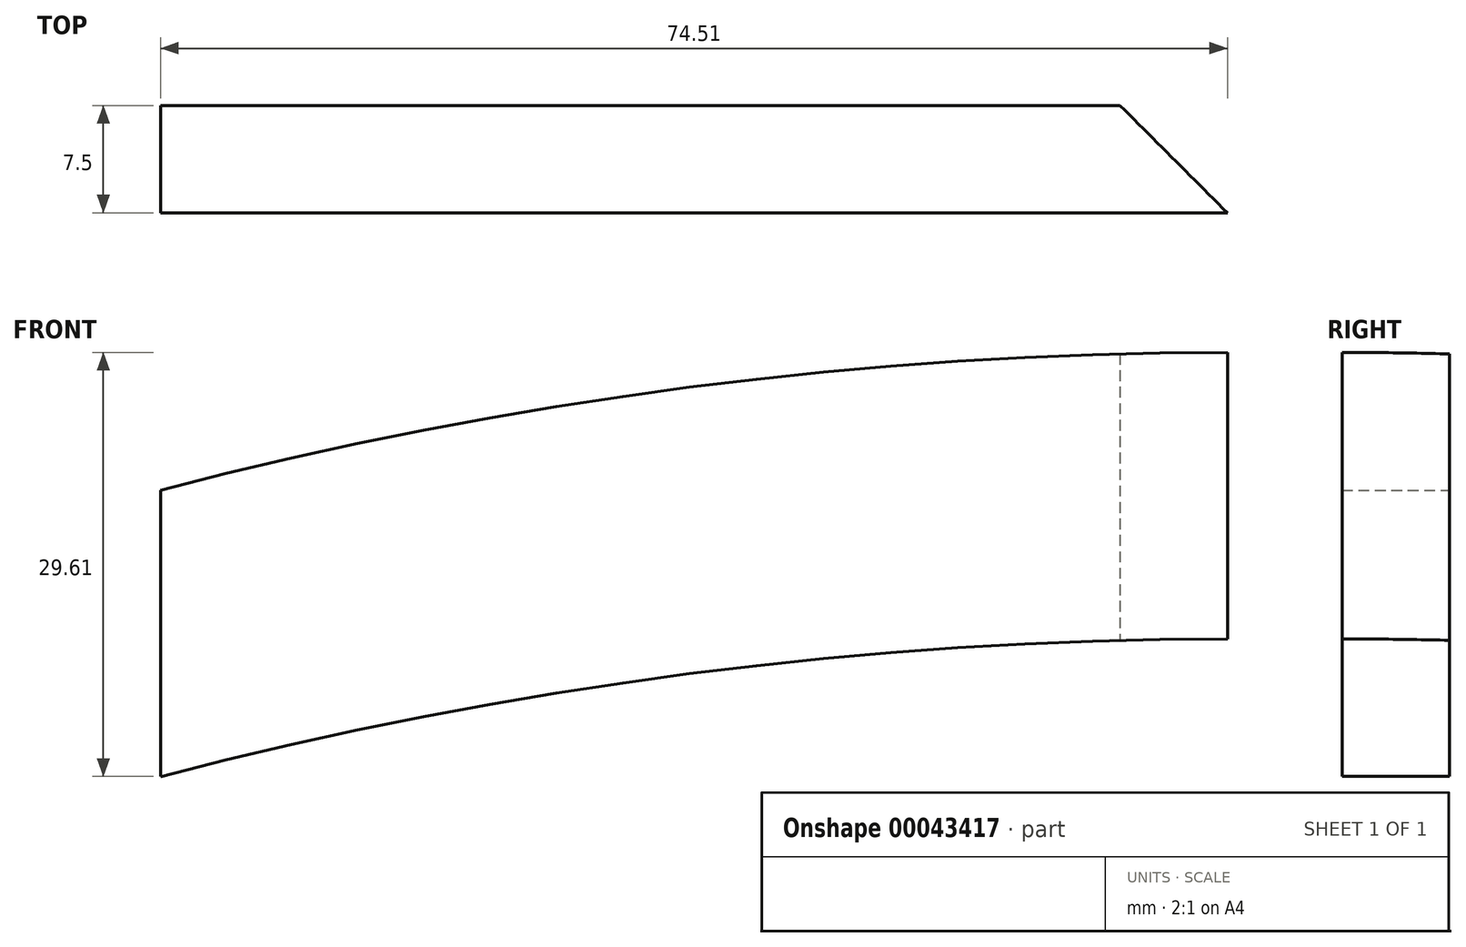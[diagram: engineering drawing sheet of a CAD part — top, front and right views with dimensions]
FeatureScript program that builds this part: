
annotation { "Feature Type Name" : "Feature", "Feature Type Description" : "" }
export const myFeature = defineFeature(function(context is Context, id is Id, definition is map)
    precondition{}
    {
        {
            var Q0;
            Q0=qCreatedBy(makeId("Front.planeOp"),FACE);
            var sketch = newSketch(context, id + "F0", { "sketchPlane" : qUnion([Q0])});
            skLineSegment(sketch, "E0", {"start": v(-75.01, 0) * mm, "end": v(-75.01, 20) * mm});
            skArc(sketch, "E1", {"start": v(0, 29.61) * mm, "mid": v(-37.81, 27.21) * mm, "end": v(-75.01, 20) * mm});
            skArc(sketch, "E2", {"start": v(0, 9.61) * mm, "mid": v(-37.81, 7.21) * mm, "end": v(-75.01, 0) * mm});
            skLineSegment(sketch, "E3", {"start": v(0, 29.61) * mm, "end": v(0, 9.61) * mm});
            skSolve(sketch);
        }
        {
            var Q0;
            {var subQ2=sQuery(id+"F0.wireOp",EDGE,"E0");Q0=makeQuery(id+"F0.imprint","IMPRINT",FACE,{"disambiguationData":[TD([[makeQuery(id+"F0.imprint","IMPRINT",EDGE,{"derivedFrom":subQ2}),-1.0]])]});}
            var Q1;
            {var subQ2=sQuery(id+"F0.wireOp",EDGE,"d5a9f697-a3c0-4d75-bb54-b9e9130054d0");Q1=makeQuery(id+"F0.imprint","IMPRINT",FACE,{"disambiguationData":[TD([[makeQuery(id+"F0.imprint","IMPRINT",EDGE,{"derivedFrom":subQ2}),1.0]])]});}
            extrude(context, id + "F1", {"entities" : qUnion([Q0, Q1]), "depth" : 7.5 * mm});
        }
        {
            var Q0;
            Q0=makeQuery(id+"F1.opExtrude","CAP_EDGE",EDGE,{"disambiguationData":[OSD([sQuery(id+"F0.wireOp",EDGE,"E3")])],"isStart":true});
            chamfer(context, id + "F2", {"entities" : qUnion([Q0]), "width" : 8 * mm, "tangentPropagation" : true});
        }
    });
